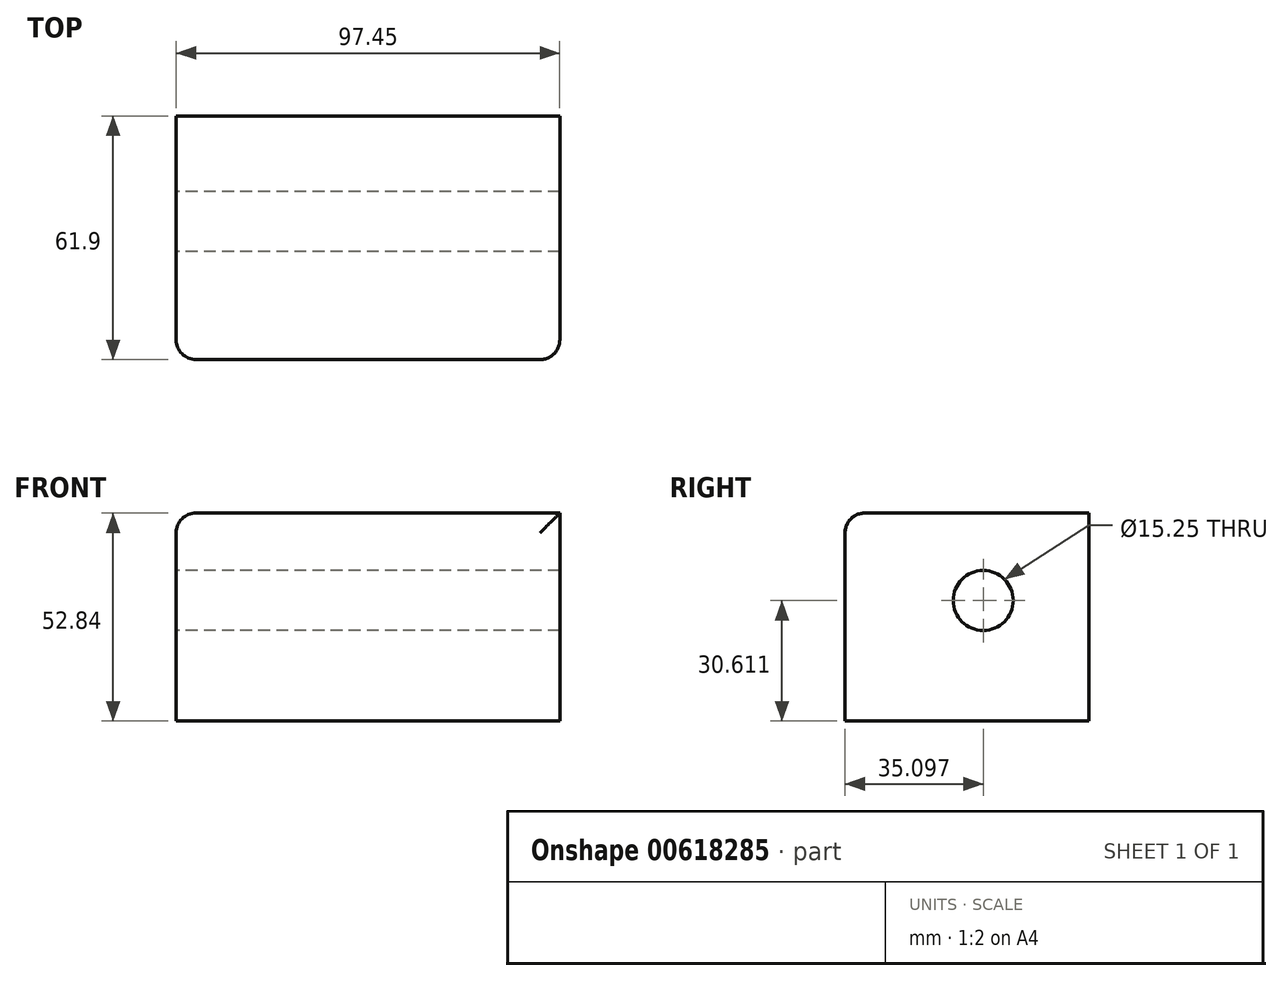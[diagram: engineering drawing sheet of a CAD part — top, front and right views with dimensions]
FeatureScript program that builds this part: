
annotation { "Feature Type Name" : "Feature", "Feature Type Description" : "" }
export const myFeature = defineFeature(function(context is Context, id is Id, definition is map)
    precondition{}
    {
        {
            var Q0;
            Q0=qCreatedBy(makeId("Front.planeOp"),FACE);
            var sketch = newSketch(context, id + "F0", { "sketchPlane" : qUnion([Q0])});
            skLineSegment(sketch, "E0.bottom", {"start": v(-60.9, -22.73) * mm, "end": v(36.54, -22.73) * mm});
            skLineSegment(sketch, "E0.top", {"start": v(-60.9, 30.1) * mm, "end": v(36.54, 30.1) * mm});
            skLineSegment(sketch, "E0.left", {"start": v(-60.9, -22.73) * mm, "end": v(-60.9, 30.1) * mm});
            skLineSegment(sketch, "E0.right", {"start": v(36.54, -22.73) * mm, "end": v(36.54, 30.1) * mm});
            skSolve(sketch);
        }
        {
            var Q0;
            Q0=makeQuery(id+"F0.imprint","IMPRINT",FACE,{"disambiguationData":[TD([[makeQuery(id+"F0.imprint","IMPRINT",EDGE,{"derivedFrom":sQuery(id+"F0.wireOp",EDGE,"E0.bottom")}),1.0]])]});
            extrude(context, id + "F1", {"entities" : qUnion([Q0]), "depth" : 61.9 * mm, "offsetDistance" : 25 * mm});
        }
        {
            var Q0;
            Q0=makeQuery(id+"F1.opExtrude","SWEPT_FACE",FACE,{"disambiguationData":[OSD([sQuery(id+"F0.wireOp",EDGE,"E0.left")])]});
            var sketch = newSketch(context, id + "F2", { "sketchPlane" : qUnion([Q0])});
            skCircle(sketch, "E1", {"center": v(26.8, 7.88) * mm, "radius": 7.62 * mm});
            skSolve(sketch);
        }
        {
            var Q0;
            Q0=makeQuery(id+"F2.imprint","IMPRINT",FACE,{"disambiguationData":[TD([[makeQuery(id+"F2.imprint","IMPRINT",EDGE,{"derivedFrom":sQuery(id+"F2.wireOp",EDGE,"E1")}),1.0]])]});
            var Q1;
            Q1=sQuery(id+"F2.wireOp",EDGE,"E1");
            extrude(context, id + "F3", {"entities" : qUnion([Q0]), "operationType" : NewBodyOperationType.REMOVE, "surfaceEntities" : qUnion([Q1]), "endBound" : BoundingType.UP_TO_NEXT, "oppositeDirection" : true, "depth" : 97.2 * mm, "offsetDistance" : 25 * mm});
        }
        {
            var Q0;
            Q0=makeQuery(id+"F1.opExtrude","SWEPT_EDGE",EDGE,{"disambiguationData":[OSD([sQuery(id+"F0.wireOp",EDGE,"E0.top"),sQuery(id+"F0.wireOp",EDGE,"E0.left")])]});
            var Q1;
            Q1=makeQuery(id+"F1.opExtrude","CAP_EDGE",EDGE,{"disambiguationData":[OSD([sQuery(id+"F0.wireOp",EDGE,"E0.top")])],"isStart":false});
            var Q2;
            Q2=makeQuery(id+"F1.opExtrude","CAP_EDGE",EDGE,{"disambiguationData":[OSD([sQuery(id+"F0.wireOp",EDGE,"E0.left")])],"isStart":false});
            var Q3;
            Q3=makeQuery(id+"F1.opExtrude","CAP_EDGE",EDGE,{"disambiguationData":[OSD([sQuery(id+"F0.wireOp",EDGE,"E0.right")])],"isStart":false});
            fillet(context, id + "F4", {"entities" : qUnion([Q0, Q1, Q2, Q3]), "radius" : 5 * mm, "tangentPropagation" : true, "allowEdgeOverflow" : false});
        }
    });
